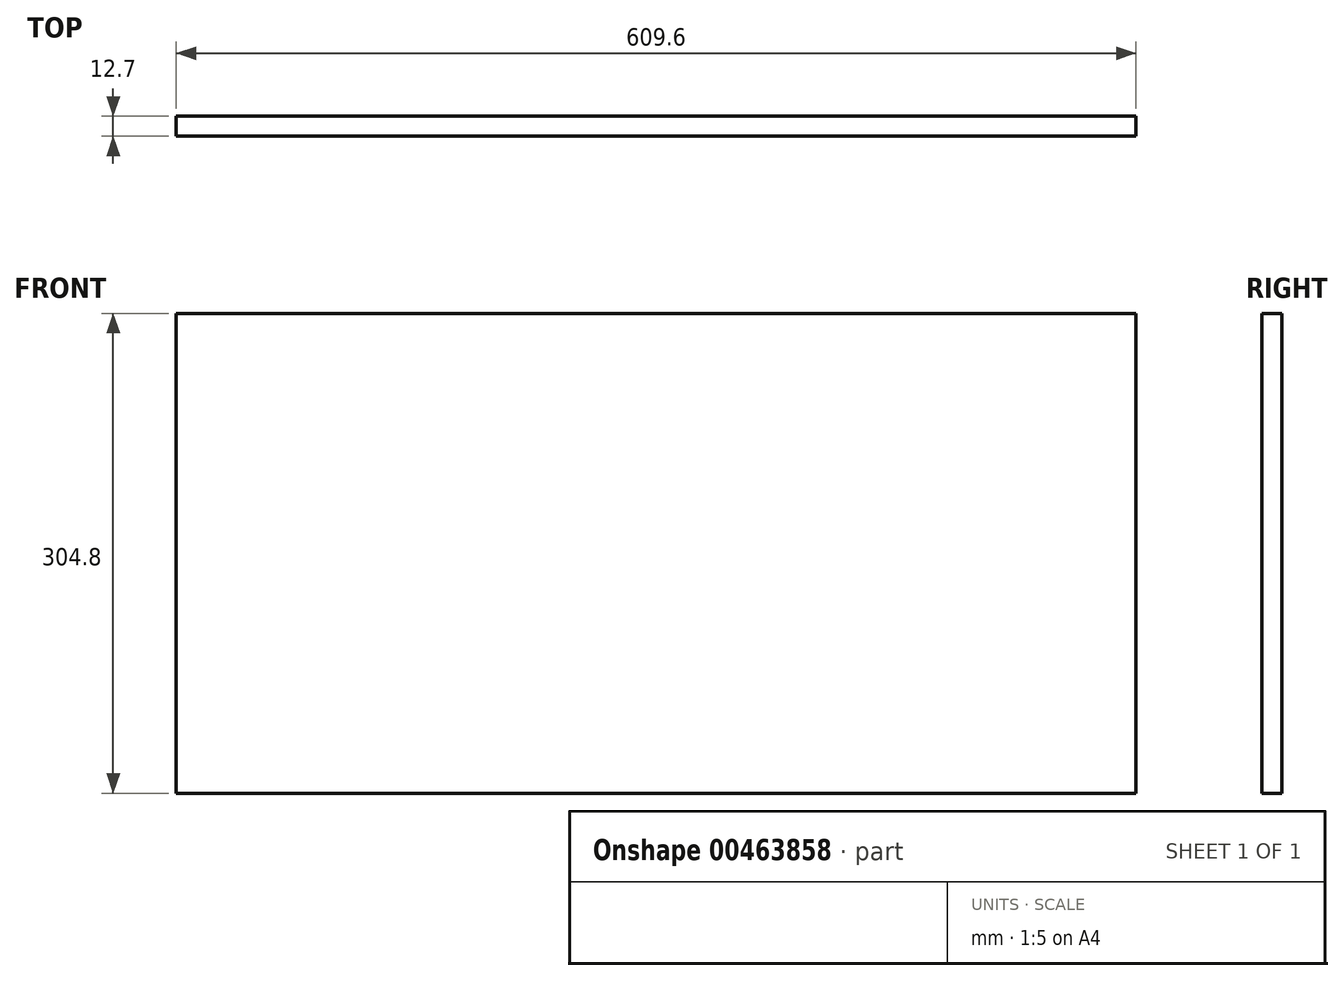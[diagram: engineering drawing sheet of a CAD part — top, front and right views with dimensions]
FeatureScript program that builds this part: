
annotation { "Feature Type Name" : "Feature", "Feature Type Description" : "" }
export const myFeature = defineFeature(function(context is Context, id is Id, definition is map)
    precondition{}
    {
        {
            var Q0;
            Q0=qCreatedBy(makeId("Front.planeOp"),FACE);
            var sketch = newSketch(context, id + "F0", { "sketchPlane" : qUnion([Q0])});
            skLineSegment(sketch, "E0.bottom", {"start": v(-503.13, 304.8) * mm, "end": v(106.47, 304.8) * mm});
            skLineSegment(sketch, "E0.top", {"start": v(-503.13, 0) * mm, "end": v(106.47, 0) * mm});
            skLineSegment(sketch, "E0.left", {"start": v(-503.13, 304.8) * mm, "end": v(-503.13, 0) * mm});
            skLineSegment(sketch, "E0.right", {"start": v(106.47, 304.8) * mm, "end": v(106.47, 0) * mm});
            skSolve(sketch);
        }
        {
            var Q0;
            Q0 = qSketchRegion(id + "F0", true);
            extrude(context, id + "F1", {"entities" : qUnion([Q0]), "depth" : 12.7 * mm});
        }
    });
